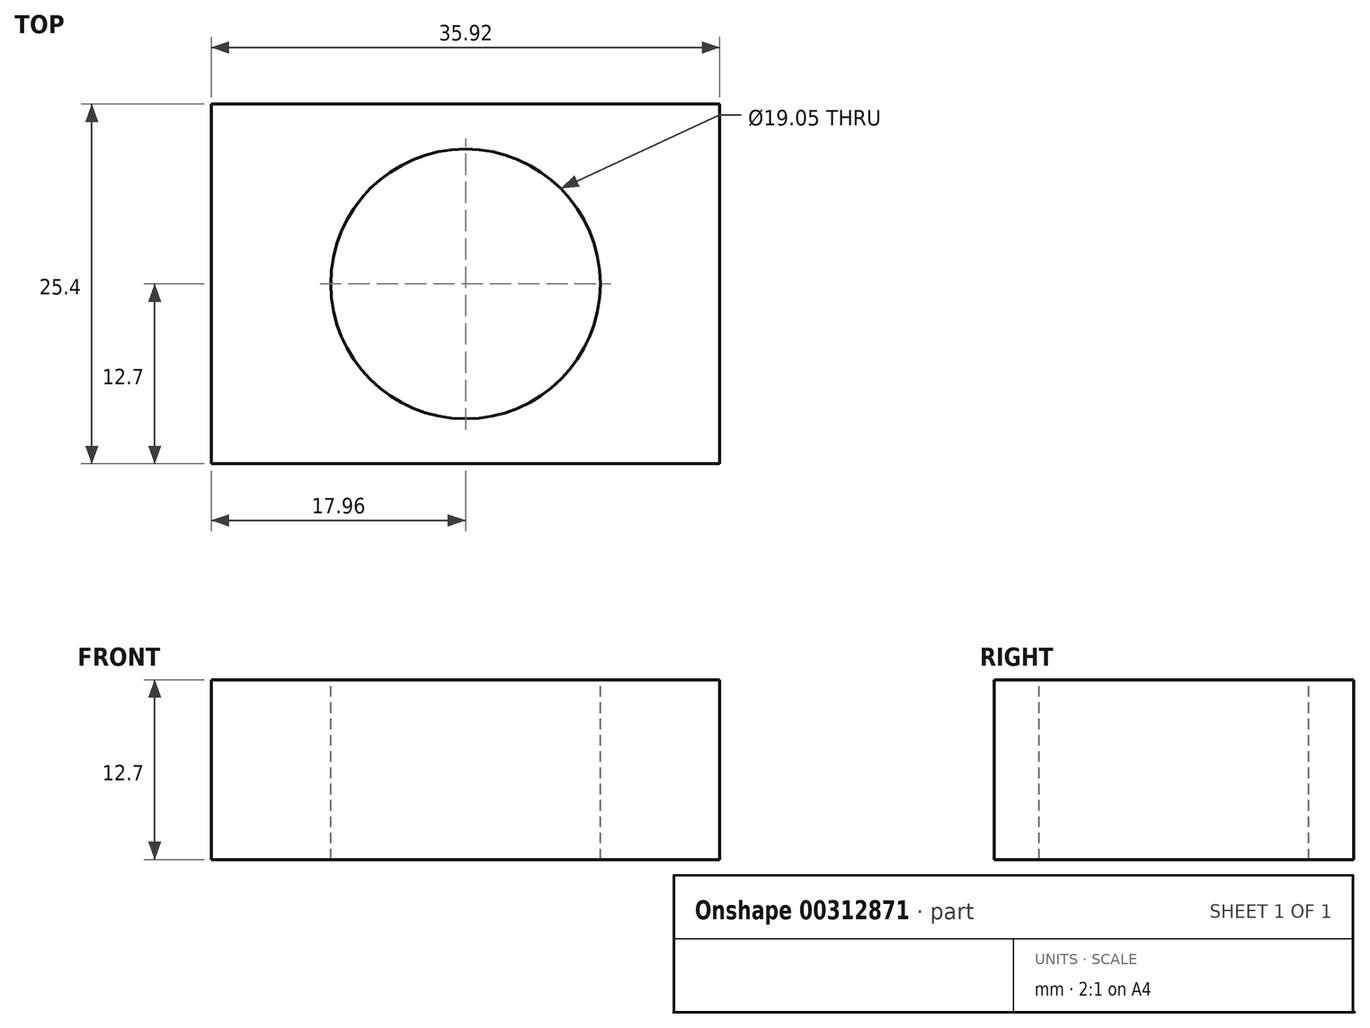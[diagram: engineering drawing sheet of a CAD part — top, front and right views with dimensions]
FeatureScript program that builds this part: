
annotation { "Feature Type Name" : "Feature", "Feature Type Description" : "" }
export const myFeature = defineFeature(function(context is Context, id is Id, definition is map)
    precondition{}
    {
        {
            var Q0;
            Q0=qCreatedBy(makeId("Front.planeOp"),FACE);
            var sketch = newSketch(context, id + "F0", { "sketchPlane" : qUnion([Q0])});
            skLineSegment(sketch, "E0.bottom", {"start": v(17.96, -6.35) * mm, "end": v(-17.96, -6.35) * mm});
            skLineSegment(sketch, "E0.top", {"start": v(17.96, 6.35) * mm, "end": v(-17.96, 6.35) * mm});
            skLineSegment(sketch, "E0.left", {"start": v(17.96, -6.35) * mm, "end": v(17.96, 6.35) * mm});
            skLineSegment(sketch, "E0.right", {"start": v(-17.96, -6.35) * mm, "end": v(-17.96, 6.35) * mm});
            skPoint(sketch, "E0.middle", {"position": v(0, 0) * mm});
            skSolve(sketch);
        }
        {
            var Q0;
            Q0 = qSketchRegion(id + "F0", true);
            extrude(context, id + "F1", {"entities" : qUnion([Q0]), "endBound" : BoundingType.SYMMETRIC, "depth" : 25.4 * mm});
        }
        {
            var Q0;
            Q0=makeQuery(id+"F1.opExtrude","SWEPT_FACE",FACE,{"disambiguationData":[OSD([sQuery(id+"F0.wireOp",EDGE,"E0.top")])]});
            var sketch = newSketch(context, id + "F2", { "sketchPlane" : qUnion([Q0])});
            skLineSegment(sketch, "E1.0.0", {"start": v(17.96, 12.7) * mm, "end": v(-17.96, 12.7) * mm});
            skLineSegment(sketch, "E1.0.1", {"start": v(-17.96, 12.7) * mm, "end": v(-17.96, -12.7) * mm});
            skLineSegment(sketch, "E1.0.2", {"start": v(-17.96, -12.7) * mm, "end": v(17.96, -12.7) * mm});
            skLineSegment(sketch, "E1.0.3", {"start": v(17.96, -12.7) * mm, "end": v(17.96, 12.7) * mm});
            skCircle(sketch, "E2", {"center": v(0, 0) * mm, "radius": 9.53 * mm});
            skSolve(sketch);
        }
        {
            var Q0;
            Q0=makeQuery(id+"F2.imprint","IMPRINT",FACE,{"disambiguationData":[TD([[makeQuery(id+"F2.imprint","IMPRINT",EDGE,{"derivedFrom":sQuery(id+"F2.wireOp",EDGE,"E2")}),1.0]])]});
            extrude(context, id + "F3", {"entities" : qUnion([Q0]), "operationType" : NewBodyOperationType.REMOVE, "endBound" : BoundingType.THROUGH_ALL, "oppositeDirection" : true, "depth" : 25.4 * mm});
        }
        {
            var Q0;
            Q0=qCreatedBy(makeId("Right.planeOp"),FACE);
            var sketch = newSketch(context, id + "F4", { "sketchPlane" : qUnion([Q0])});
            skLineSegment(sketch, "E3.0.1", {"start": v(12.7, 6.35) * mm, "end": v(-12.7, 6.35) * mm});
            skLineSegment(sketch, "E3.0.3", {"start": v(-12.7, 6.35) * mm, "end": v(12.7, 6.35) * mm});
            skLineSegment(sketch, "E4", {"start": v(-12.7, 6.35) * mm, "end": v(-25.53, 20.43) * mm});
            skLineSegment(sketch, "E5", {"start": v(0, 27.63) * mm, "end": v(0, -37.7) * mm});
            skPoint(sketch, "E5.endSnap0", {"position": v(0, 6.35) * mm});
            skSolve(sketch);
        }
        {
            var Q0;
            Q0 = qSketchRegion(id + "FMtgOnfpl4LPTuk_1", true);
            var Q1;
            Q1=sQuery(id+"F4.wireOp",EDGE,"E4");
            var Q2;
            Q2=sQuery(id+"F4.wireOp",EDGE,"E5");
            revolve(context, id + "F5", {"bodyType" : ToolBodyType.SURFACE, "entities" : qUnion([Q0]), "surfaceEntities" : qUnion([Q1]), "axis" : qUnion([Q2]), "revolveType" : RevolveType.FULL});
        }
    });
